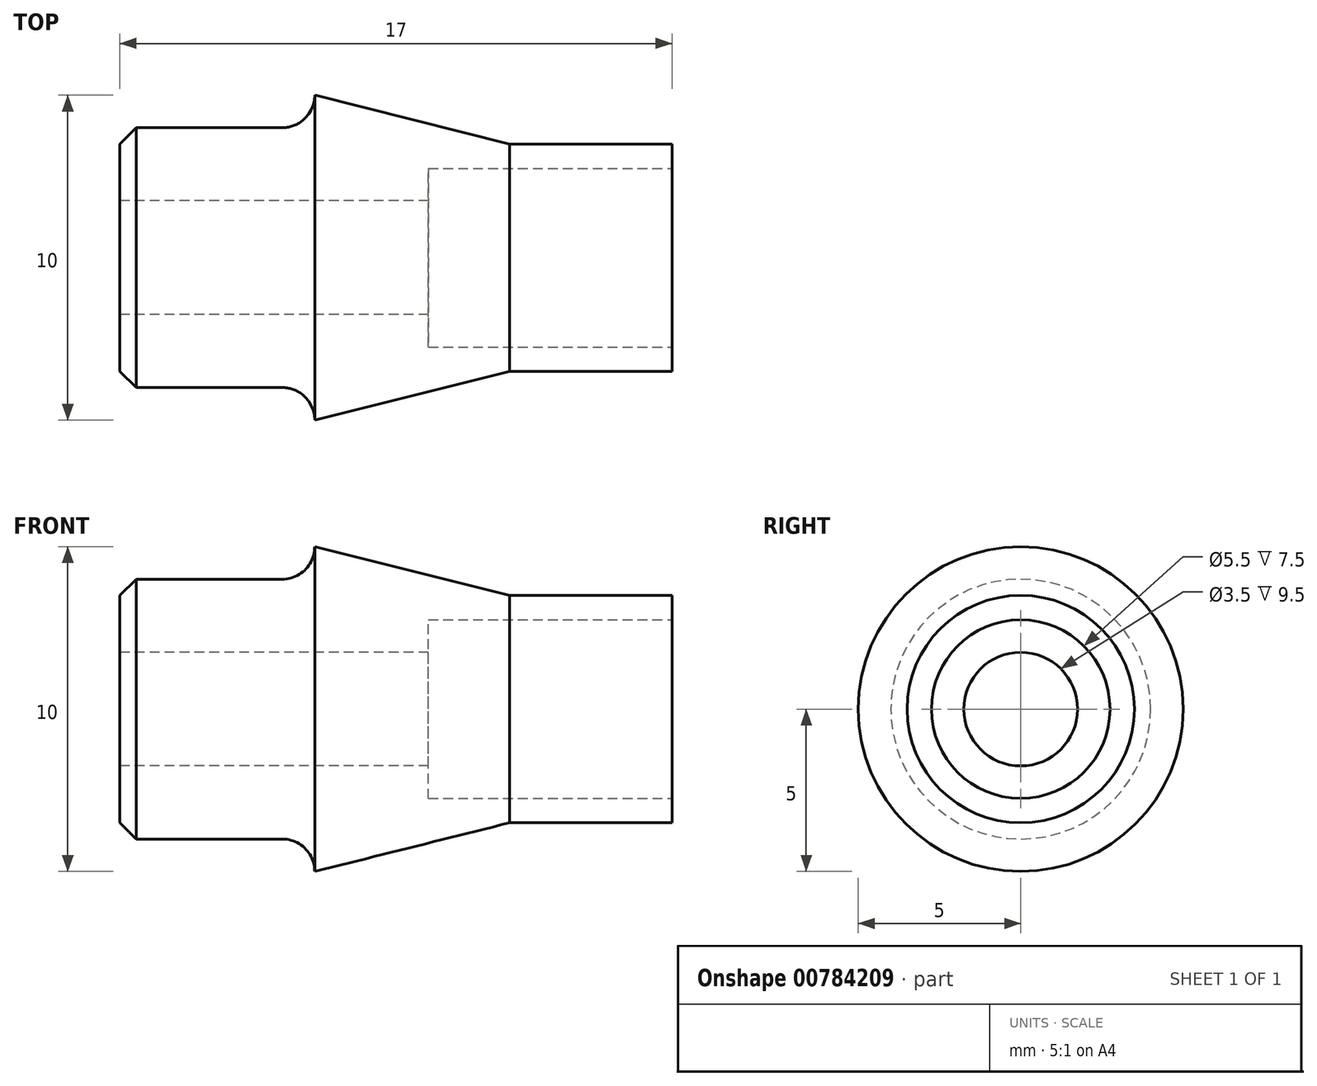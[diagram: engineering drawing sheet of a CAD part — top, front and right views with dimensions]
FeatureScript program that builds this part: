
annotation { "Feature Type Name" : "Feature", "Feature Type Description" : "" }
export const myFeature = defineFeature(function(context is Context, id is Id, definition is map)
    precondition{}
    {
        {
            var Q0;
            Q0=qCreatedBy(makeId("Front.planeOp"),FACE);
            var sketch = newSketch(context, id + "F0", { "sketchPlane" : qUnion([Q0])});
            skLineSegment(sketch, "E0", {"start": v(0, 0) * mm, "end": v(0, 4) * mm});
            skLineSegment(sketch, "E1", {"start": v(0, 4) * mm, "end": v(6, 4) * mm});
            skLineSegment(sketch, "E2", {"start": v(6, 4) * mm, "end": v(6, 5) * mm});
            skLineSegment(sketch, "E3", {"start": v(6, 5) * mm, "end": v(12, 3.5) * mm});
            skLineSegment(sketch, "E4", {"start": v(12, 3.5) * mm, "end": v(17, 3.5) * mm});
            skLineSegment(sketch, "E5", {"start": v(17, 3.5) * mm, "end": v(17, 0) * mm});
            skLineSegment(sketch, "E6", {"start": v(17, 0) * mm, "end": v(0, 0) * mm});
            skSolve(sketch);
        }
        {
            var Q0;
            Q0=makeQuery(id+"F0.imprint","IMPRINT",FACE,{"disambiguationData":[TD([[makeQuery(id+"F0.imprint","IMPRINT",EDGE,{"derivedFrom":sQuery(id+"F0.wireOp",EDGE,"E0")}),-1.0]])]});
            var Q1;
            Q1=sQuery(id+"F0.wireOp",EDGE,"E6");
            revolve(context, id + "F1", {"surfaceOperationType" : NewSurfaceOperationType.NEW, "entities" : qUnion([Q0]), "axis" : qUnion([Q1]), "revolveType" : RevolveType.FULL});
        }
        {
            var Q0;
            Q0=makeQuery(id+"F1.opRevolve","SWEPT_EDGE",EDGE,{"disambiguationData":[OSD([sQuery(id+"F0.wireOp",EDGE,"E1"),sQuery(id+"F0.wireOp",EDGE,"E2")])]});
            fillet(context, id + "F2", {"entities" : qUnion([Q0]), "radius" : 1 * mm, "tangentPropagation" : true, "allowEdgeOverflow" : false});
        }
        {
            var Q0;
            Q0=makeQuery(id+"F1.opRevolve","SWEPT_FACE",FACE,{"disambiguationData":[OSD([sQuery(id+"F0.wireOp",EDGE,"E5")])]});
            var sketch = newSketch(context, id + "F3", { "sketchPlane" : qUnion([Q0])});
            skCircle(sketch, "E7", {"center": v(0, 0) * mm, "radius": 2.75 * mm});
            skSolve(sketch);
        }
        {
            var Q0;
            Q0=makeQuery(id+"F3.imprint","IMPRINT",FACE,{"disambiguationData":[TD([[makeQuery(id+"F3.imprint","IMPRINT",EDGE,{"derivedFrom":sQuery(id+"F3.wireOp",EDGE,"E7")}),1.0]])]});
            extrude(context, id + "F4", {"entities" : qUnion([Q0]), "operationType" : NewBodyOperationType.REMOVE, "oppositeDirection" : true, "depth" : 7.5 * mm, "offsetDistance" : 25 * mm});
        }
        {
            var Q0;
            Q0=makeQuery(id+"F1.opRevolve","SWEPT_FACE",FACE,{"disambiguationData":[OSD([sQuery(id+"F0.wireOp",EDGE,"E0")])]});
            var sketch = newSketch(context, id + "F5", { "sketchPlane" : qUnion([Q0])});
            skCircle(sketch, "E8", {"center": v(0, 0) * mm, "radius": 1.75 * mm});
            skSolve(sketch);
        }
        {
            var Q0;
            Q0=makeQuery(id+"F5.imprint","IMPRINT",FACE,{"disambiguationData":[TD([[makeQuery(id+"F5.imprint","IMPRINT",EDGE,{"derivedFrom":sQuery(id+"F5.wireOp",EDGE,"E8")}),1.0]])]});
            extrude(context, id + "F6", {"entities" : qUnion([Q0]), "operationType" : NewBodyOperationType.REMOVE, "endBound" : BoundingType.UP_TO_NEXT, "oppositeDirection" : true, "depth" : 25 * mm, "offsetDistance" : 25 * mm});
        }
        {
            var Q0;
            Q0=makeQuery(id+"F1.opRevolve","SWEPT_EDGE",EDGE,{"disambiguationData":[OSD([sQuery(id+"F0.wireOp",EDGE,"E0"),sQuery(id+"F0.wireOp",EDGE,"E1")])]});
            var Q1;
            Q1=makeQuery(id+"F6.boolean.opBoolean","COPY",EDGE,{"derivedFrom":makeQuery(id+"F6.opExtrude","CAP_EDGE",EDGE,{"disambiguationData":[OSD([sQuery(id+"F5.wireOp",EDGE,"E8")])],"isStart":true})});
            chamfer(context, id + "F7", {"entities" : qUnion([Q0, Q1]), "width" : 0.5 * mm, "tangentPropagation" : true});
        }
    });
